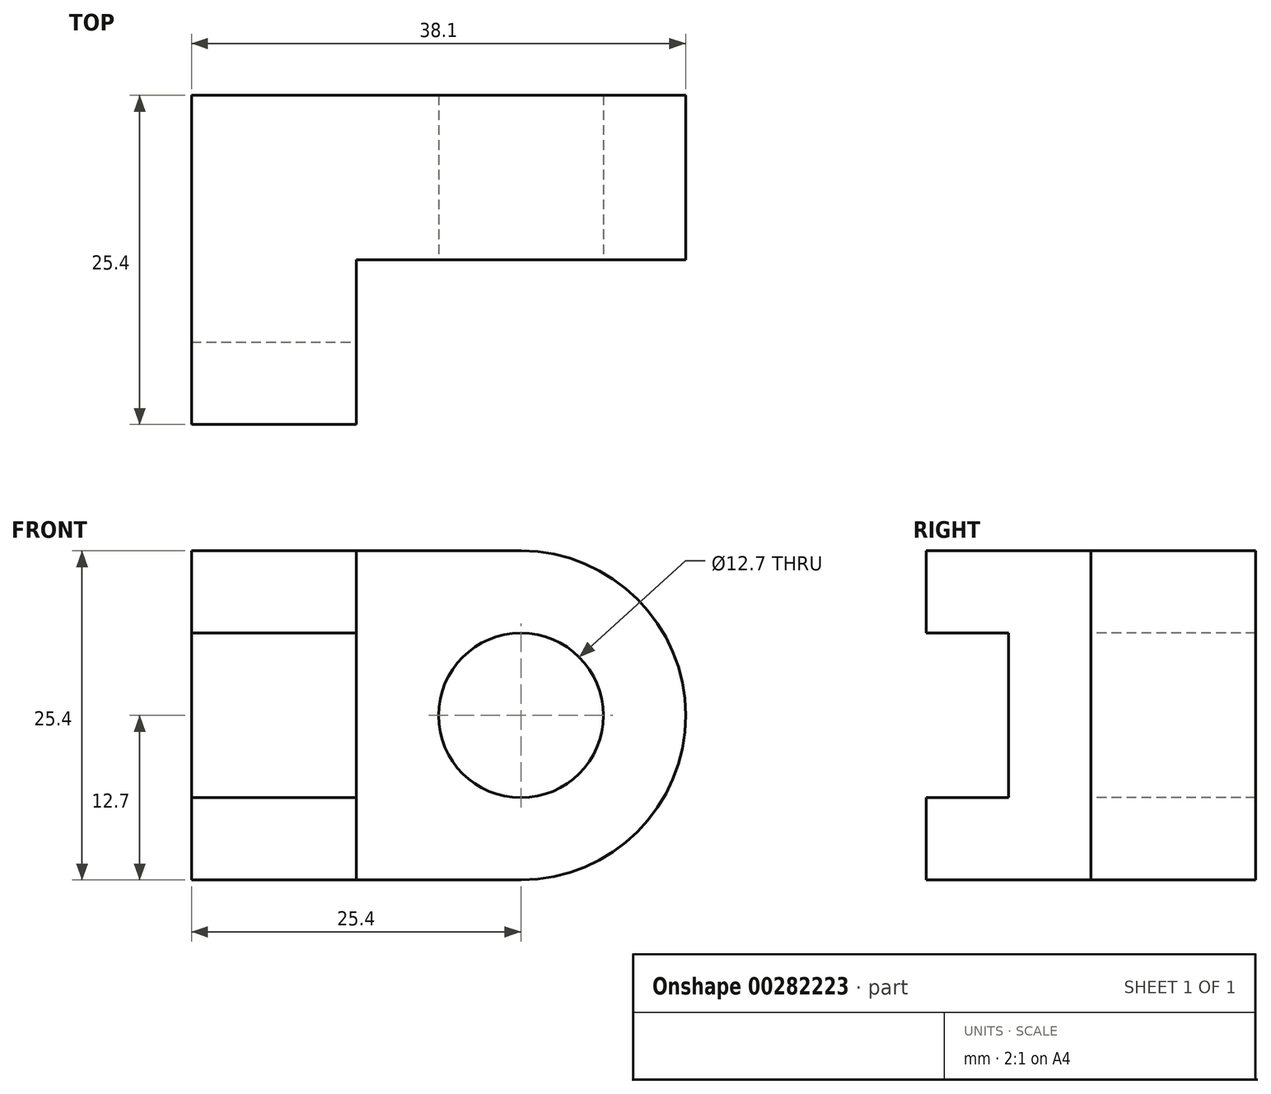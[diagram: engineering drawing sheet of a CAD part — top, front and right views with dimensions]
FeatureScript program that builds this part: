
annotation { "Feature Type Name" : "Feature", "Feature Type Description" : "" }
export const myFeature = defineFeature(function(context is Context, id is Id, definition is map)
    precondition{}
    {
        {
            var Q0;
            Q0=qCreatedBy(makeId("Front.planeOp"),FACE);
            var sketch = newSketch(context, id + "F0", { "sketchPlane" : qUnion([Q0])});
            skLineSegment(sketch, "E0.bottom", {"start": v(0, 0) * mm, "end": v(25.4, 0) * mm});
            skLineSegment(sketch, "E0.top", {"start": v(0, 25.4) * mm, "end": v(25.4, 25.4) * mm});
            skLineSegment(sketch, "E0.left", {"start": v(0, 0) * mm, "end": v(0, 25.4) * mm});
            skArc(sketch, "E1", {"start": v(25.4, 0) * mm, "mid": v(38.1, 12.7) * mm, "end": v(25.4, 25.4) * mm});
            skLineSegment(sketch, "E2", {"start": v(25.4, 25.4) * mm, "end": v(25.4, 0) * mm, "construction": true});
            skSolve(sketch);
        }
        {
            var Q0;
            Q0=makeQuery(id+"F0.imprint","IMPRINT",FACE,{"disambiguationData":[TD([[makeQuery(id+"F0.imprint","IMPRINT",EDGE,{"derivedFrom":sQuery(id+"F0.wireOp",EDGE,"E0.bottom")}),1.0]])]});
            extrude(context, id + "F1", {"entities" : qUnion([Q0]), "depth" : 12.7 * mm});
        }
        {
            var Q0;
            Q0=makeQuery(id+"F1.opExtrude","CAP_FACE",FACE,{"disambiguationData":[OSD([sQuery(id+"F0.wireOp",EDGE,"E0.bottom"),sQuery(id+"F0.wireOp",EDGE,"E0.top"),sQuery(id+"F0.wireOp",EDGE,"E0.left"),sQuery(id+"F0.wireOp",EDGE,"E1")])],"isStart":false});
            var sketch = newSketch(context, id + "F2", { "sketchPlane" : qUnion([Q0])});
            skLineSegment(sketch, "E3.bottom", {"start": v(0, 0) * mm, "end": v(12.7, 0) * mm});
            skLineSegment(sketch, "E3.top", {"start": v(0, 25.4) * mm, "end": v(12.7, 25.4) * mm});
            skLineSegment(sketch, "E3.left", {"start": v(0, 0) * mm, "end": v(0, 25.4) * mm});
            skLineSegment(sketch, "E3.right", {"start": v(12.7, 0) * mm, "end": v(12.7, 25.4) * mm});
            skSolve(sketch);
        }
        {
            var Q0;
            Q0=makeQuery(id+"F2.imprint","IMPRINT",FACE,{"disambiguationData":[TD([[makeQuery(id+"F2.imprint","IMPRINT",EDGE,{"derivedFrom":sQuery(id+"F2.wireOp",EDGE,"E3.bottom")}),1.0]])]});
            extrude(context, id + "F3", {"entities" : qUnion([Q0]), "operationType" : NewBodyOperationType.ADD, "depth" : 12.7 * mm});
        }
        {
            var Q0;
            Q0=makeQuery(id+"F3.opExtrude","CAP_FACE",FACE,{"disambiguationData":[OSD([sQuery(id+"F2.wireOp",EDGE,"E3.bottom"),sQuery(id+"F2.wireOp",EDGE,"E3.top"),sQuery(id+"F2.wireOp",EDGE,"E3.left"),sQuery(id+"F2.wireOp",EDGE,"E3.right")])],"isStart":false});
            var sketch = newSketch(context, id + "F4", { "sketchPlane" : qUnion([Q0])});
            skLineSegment(sketch, "E4.bottom", {"start": v(0, 19.05) * mm, "end": v(12.7, 19.05) * mm});
            skLineSegment(sketch, "E4.top", {"start": v(0, 6.35) * mm, "end": v(12.7, 6.35) * mm});
            skLineSegment(sketch, "E4.left", {"start": v(0, 19.05) * mm, "end": v(0, 6.35) * mm});
            skLineSegment(sketch, "E4.right", {"start": v(12.7, 19.05) * mm, "end": v(12.7, 6.35) * mm});
            skSolve(sketch);
        }
        {
            var Q0;
            Q0=makeQuery(id+"F4.imprint","IMPRINT",FACE,{"disambiguationData":[TD([[makeQuery(id+"F4.imprint","IMPRINT",EDGE,{"derivedFrom":sQuery(id+"F4.wireOp",EDGE,"E4.bottom")}),-1.0]])]});
            extrude(context, id + "F5", {"entities" : qUnion([Q0]), "operationType" : NewBodyOperationType.REMOVE, "oppositeDirection" : true, "depth" : 6.35 * mm});
        }
        {
            var Q0;
            Q0=makeQuery(id+"F1.opExtrude","CAP_FACE",FACE,{"disambiguationData":[OSD([sQuery(id+"F0.wireOp",EDGE,"E0.bottom"),sQuery(id+"F0.wireOp",EDGE,"E0.top"),sQuery(id+"F0.wireOp",EDGE,"E0.left"),sQuery(id+"F0.wireOp",EDGE,"E1")])],"isStart":false});
            var sketch = newSketch(context, id + "F6", { "sketchPlane" : qUnion([Q0])});
            skCircle(sketch, "E5", {"center": v(25.4, 12.7) * mm, "radius": 6.35 * mm});
            skSolve(sketch);
        }
        {
            var Q0;
            Q0=makeQuery(id+"F6.imprint","IMPRINT",FACE,{"disambiguationData":[TD([[makeQuery(id+"F6.imprint","IMPRINT",EDGE,{"derivedFrom":sQuery(id+"F6.wireOp",EDGE,"E5")}),1.0]])]});
            extrude(context, id + "F7", {"entities" : qUnion([Q0]), "operationType" : NewBodyOperationType.REMOVE, "endBound" : BoundingType.THROUGH_ALL, "oppositeDirection" : true, "depth" : 25.4 * mm});
        }
    });
